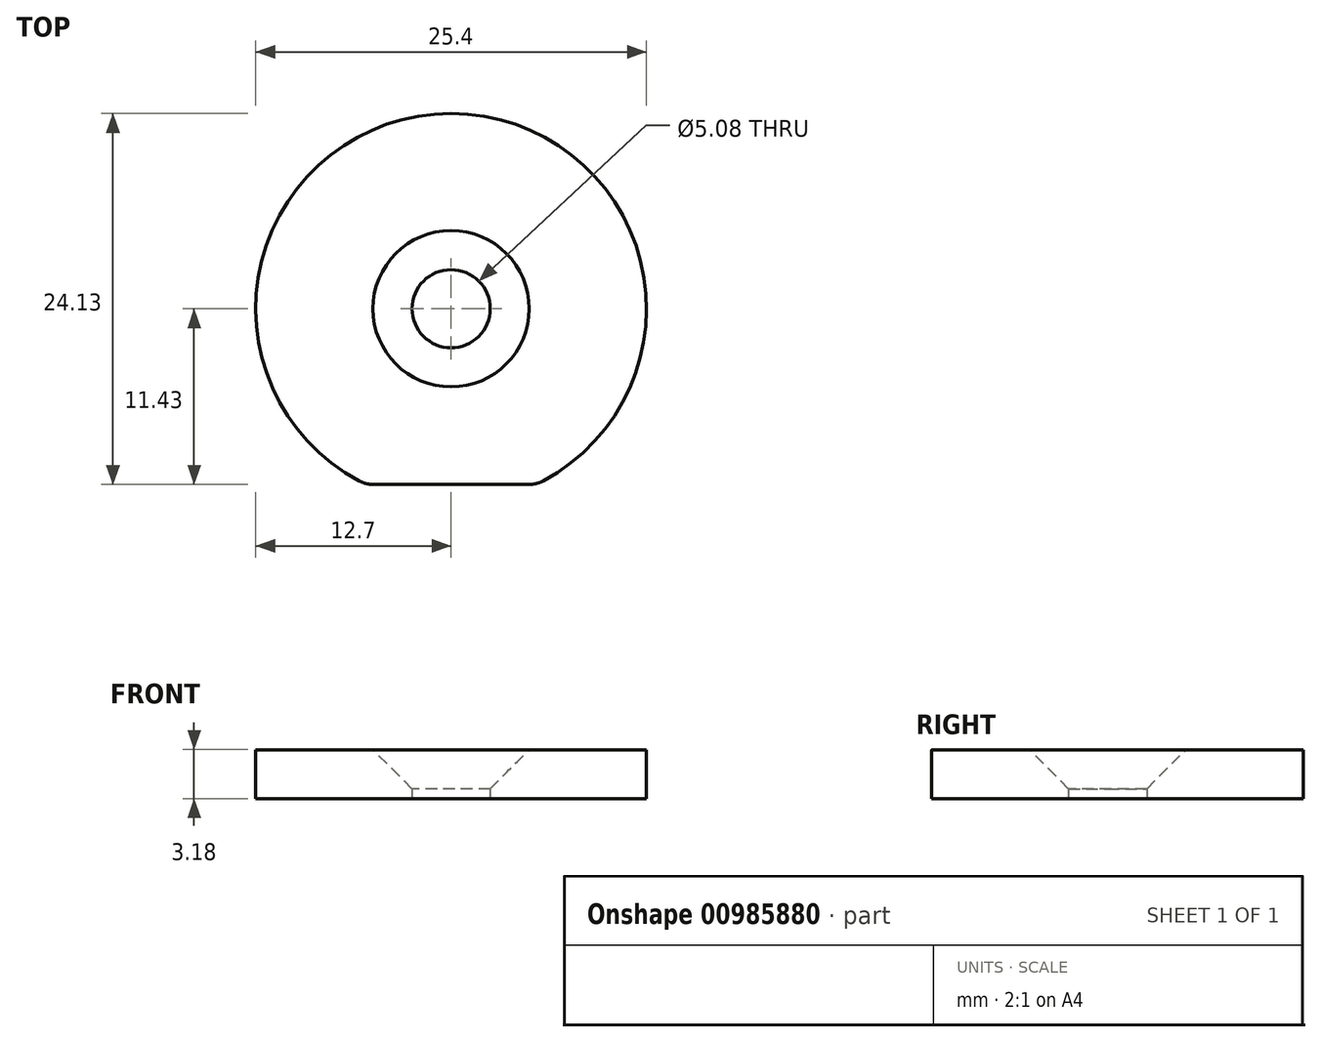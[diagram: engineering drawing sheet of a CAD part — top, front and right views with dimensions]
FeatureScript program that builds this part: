
annotation { "Feature Type Name" : "Feature", "Feature Type Description" : "" }
export const myFeature = defineFeature(function(context is Context, id is Id, definition is map)
    precondition{}
    {
        {
            var Q0;
            Q0=qCreatedBy(makeId("Top.planeOp"),FACE);
            var sketch = newSketch(context, id + "F0", { "sketchPlane" : qUnion([Q0])});
            skCircle(sketch, "E0", {"center": v(0, 0) * mm, "radius": 12.7 * mm});
            skCircle(sketch, "E1", {"center": v(0, 0) * mm, "radius": 2.54 * mm});
            skLineSegment(sketch, "E2", {"start": v(-5.54, -11.43) * mm, "end": v(5.54, -11.43) * mm});
            skSolve(sketch);
        }
        {
            var Q0;
            Q0=makeQuery(id+"F0.imprint","IMPRINT",FACE,{"disambiguationData":[TD([[makeQuery(id+"F0.imprint","IMPRINT",EDGE,{"derivedFrom":sQuery(id+"F0.wireOp",EDGE,"E1")}),-1.0]])]});
            extrude(context, id + "F1", {"entities" : qUnion([Q0]), "depth" : 3.17 * mm, "offsetDistance" : 25.4 * mm});
        }
        {
            var Q0;
            Q0=makeQuery(id+"F1.opExtrude","CAP_EDGE",EDGE,{"disambiguationData":[OSD([sQuery(id+"F0.wireOp",EDGE,"E1")])],"isStart":false});
            chamfer(context, id + "F2", {"entities" : qUnion([Q0]), "chamferType" : ChamferType.TWO_OFFSETS, "width1" : 2.54 * mm, "oppositeDirection" : false, "width2" : 2.54 * mm, "tangentPropagation" : true});
        }
        {
            var Q0;
            {var subQ0=sQuery(id+"F0.wireOp",EDGE,"E2");var subQ1=sQuery(id+"F0.wireOp",EDGE,"E0");Q0=makeQuery(id+"F1.opExtrude","SWEPT_EDGE",EDGE,{"disambiguationData":[OSD([subQ1,subQ0]),TDD([makeQuery(id+"F0.imprint","INTERSECT",VERTEX,{"disambiguationData":[OD(1.0)],"derivedFrom":[subQ1,subQ0]})])]});}
            var Q1;
            {var subQ0=sQuery(id+"F0.wireOp",EDGE,"E2");var subQ1=sQuery(id+"F0.wireOp",EDGE,"E0");Q1=makeQuery(id+"F1.opExtrude","SWEPT_EDGE",EDGE,{"disambiguationData":[OSD([subQ1,subQ0]),TDD([makeQuery(id+"F0.imprint","INTERSECT",VERTEX,{"disambiguationData":[OD(0.0)],"derivedFrom":[subQ1,subQ0]})])]});}
            fillet(context, id + "F3", {"entities" : qUnion([Q0, Q1]), "radius" : 1.9 * mm, "tangentPropagation" : true, "allowEdgeOverflow" : false});
        }
    });
